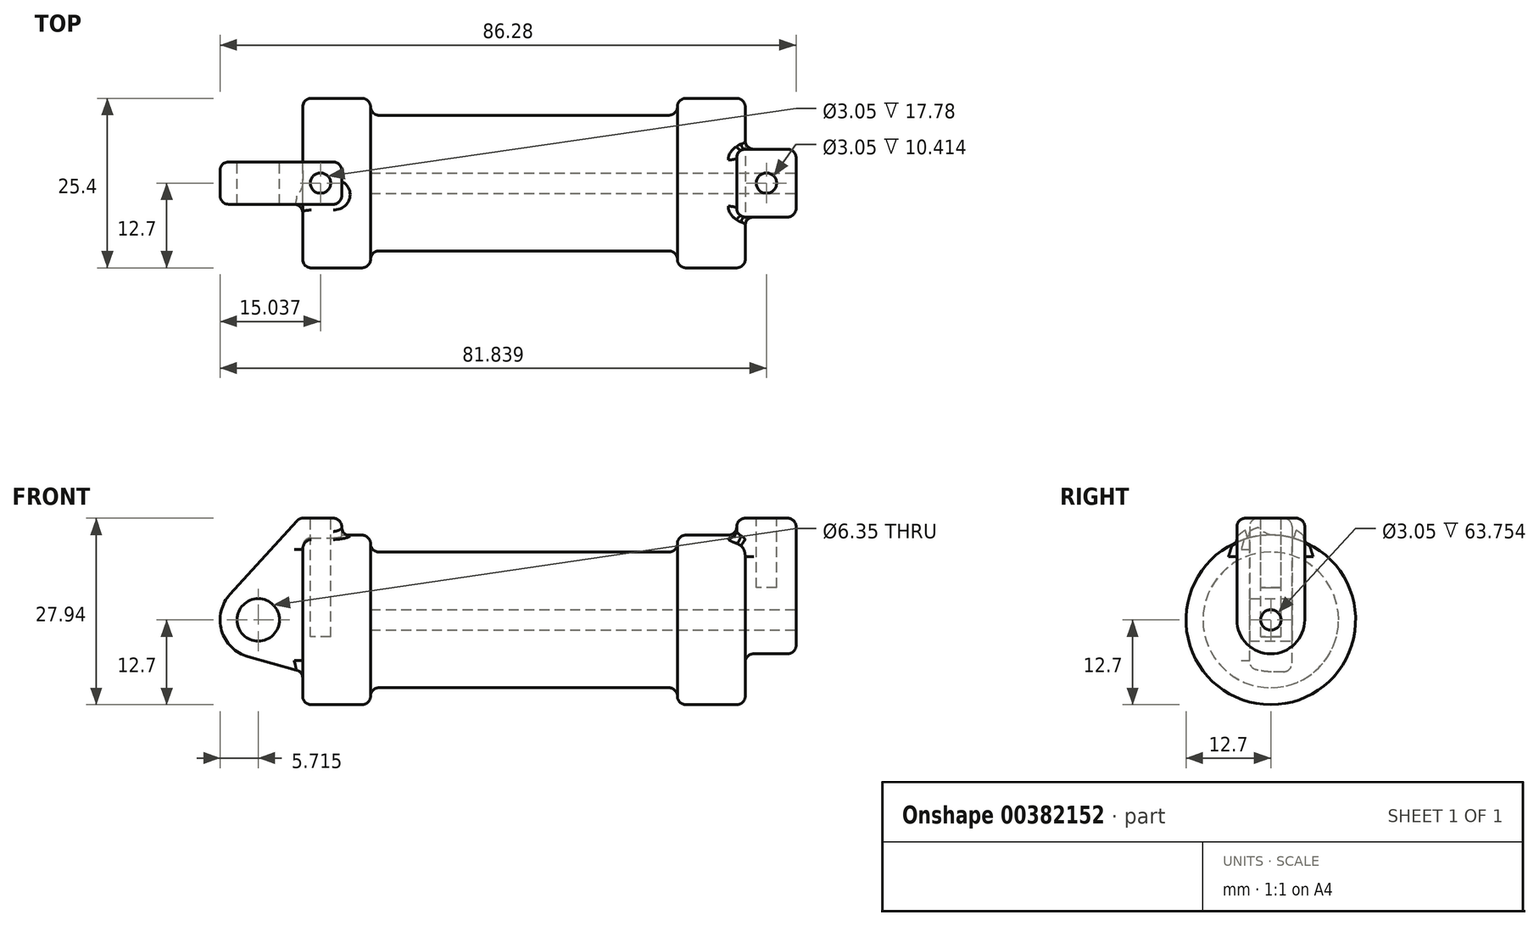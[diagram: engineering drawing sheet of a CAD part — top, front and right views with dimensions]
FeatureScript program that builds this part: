
annotation { "Feature Type Name" : "Feature", "Feature Type Description" : "" }
export const myFeature = defineFeature(function(context is Context, id is Id, definition is map)
    precondition{}
    {
        {
            var Q0;
            Q0=qCreatedBy(makeId("Front.planeOp"),FACE);
            var sketch = newSketch(context, id + "F0", { "sketchPlane" : qUnion([Q0])});
            skLineSegment(sketch, "E0", {"start": v(0, 0) * mm, "end": v(0, 12.7) * mm});
            skLineSegment(sketch, "E1", {"start": v(0, 12.7) * mm, "end": v(10.16, 12.7) * mm});
            skLineSegment(sketch, "E2", {"start": v(10.16, 12.7) * mm, "end": v(10.16, 10.16) * mm});
            skLineSegment(sketch, "E3", {"start": v(10.16, 10.16) * mm, "end": v(56.13, 10.16) * mm});
            skLineSegment(sketch, "E4", {"start": v(56.13, 10.16) * mm, "end": v(56.13, 12.7) * mm});
            skLineSegment(sketch, "E5", {"start": v(56.13, 12.7) * mm, "end": v(66.3, 12.7) * mm});
            skLineSegment(sketch, "E6", {"start": v(66.3, 12.7) * mm, "end": v(66.3, 0) * mm});
            skLineSegment(sketch, "E7", {"start": v(66.3, 0) * mm, "end": v(0, 0) * mm});
            skLineSegment(sketch, "E8", {"start": v(5.84, 15.24) * mm, "end": v(-0.5, 15.24) * mm});
            skLineSegment(sketch, "E9", {"start": v(-0.5, 15.24) * mm, "end": v(-10.88, 3.85) * mm});
            skLineSegment(sketch, "E10", {"start": v(0, 0) * mm, "end": v(-6.65, 0) * mm});
            skCircle(sketch, "E11", {"center": v(-6.65, 0) * mm, "radius": 5.72 * mm});
            skCircle(sketch, "E12", {"center": v(-6.65, 0) * mm, "radius": 3.18 * mm});
            skLineSegment(sketch, "E13", {"start": v(5.84, 15.24) * mm, "end": v(5.84, -9.4) * mm});
            skLineSegment(sketch, "E14", {"start": v(5.84, -9.4) * mm, "end": v(-8.18, -5.5) * mm});
            skSolve(sketch);
        }
        {
            var Q0;
            {var subQ1=sQuery(id+"F0.wireOp",EDGE,"E0");Q0=makeQuery(id+"F0.imprint","IMPRINT",FACE,{"disambiguationData":[TD([[makeQuery(id+"F0.imprint","IMPRINT",EDGE,{"derivedFrom":subQ1}),1.0]])]});}
            var Q1;
            {var subQ0=sQuery(id+"F0.wireOp",EDGE,"E14");Q1=makeQuery(id+"F0.imprint","IMPRINT",FACE,{"disambiguationData":[TD([[makeQuery(id+"F0.imprint","IMPRINT",EDGE,{"derivedFrom":subQ0}),-1.0]])]});}
            var Q2;
            {var subQ5=sQuery(id+"F0.wireOp",EDGE,"E12");Q2=makeQuery(id+"F0.imprint","IMPRINT",FACE,{"disambiguationData":[TD([[makeQuery(id+"F0.imprint","IMPRINT",EDGE,{"derivedFrom":subQ5}),-1.0]])]});}
            var Q3;
            {var subQ0=sQuery(id+"F0.wireOp",EDGE,"E0");Q3=makeQuery(id+"F0.imprint","IMPRINT",FACE,{"disambiguationData":[TD([[makeQuery(id+"F0.imprint","IMPRINT",EDGE,{"derivedFrom":subQ0}),-1.0]])]});}
            extrude(context, id + "F1", {"entities" : qUnion([Q0, Q1, Q2, Q3]), "endBound" : BoundingType.SYMMETRIC, "depth" : 6.35 * mm});
        }
        {
            var Q0;
            {var subQ0=sQuery(id+"F0.wireOp",EDGE,"E0");Q0=makeQuery(id+"F0.imprint","IMPRINT",FACE,{"disambiguationData":[TD([[makeQuery(id+"F0.imprint","IMPRINT",EDGE,{"derivedFrom":subQ0}),-1.0]])]});}
            var Q1;
            {var subQ0=sQuery(id+"F0.wireOp",EDGE,"E2");Q1=makeQuery(id+"F0.imprint","IMPRINT",FACE,{"disambiguationData":[TD([[makeQuery(id+"F0.imprint","IMPRINT",EDGE,{"derivedFrom":subQ0}),-1.0]])]});}
            var Q2;
            Q2=sQuery(id+"F0.wireOp",EDGE,"E7");
            revolve(context, id + "F2", {"operationType" : NewBodyOperationType.ADD, "entities" : qUnion([Q0, Q1]), "axis" : qUnion([Q2]), "revolveType" : RevolveType.FULL});
        }
        {
            var Q0;
            Q0=makeQuery(id+"F2.opRevolve","SWEPT_FACE",FACE,{"disambiguationData":[OSD([sQuery(id+"F0.wireOp",EDGE,"E6")])]});
            var sketch = newSketch(context, id + "F3", { "sketchPlane" : qUnion([Q0])});
            skCircle(sketch, "E15", {"center": v(0, 0) * mm, "radius": 1.52 * mm});
            skCircle(sketch, "E16", {"center": v(0, 0) * mm, "radius": 5.08 * mm});
            skLineSegment(sketch, "E17", {"start": v(-5.08, 0) * mm, "end": v(-5.08, 15.24) * mm});
            skLineSegment(sketch, "E18", {"start": v(5.08, 0) * mm, "end": v(5.08, 15.24) * mm});
            skLineSegment(sketch, "E19", {"start": v(5.08, 15.24) * mm, "end": v(-5.08, 15.24) * mm});
            skSolve(sketch);
        }
        {
            var Q0;
            Q0=makeQuery(id+"F3.imprint","IMPRINT",FACE,{"disambiguationData":[TD([[makeQuery(id+"F3.imprint","IMPRINT",EDGE,{"derivedFrom":sQuery(id+"F3.wireOp",EDGE,"E15")}),1.0]])]});
            var Q1;
            Q1=sQuery(id+"F3.wireOp",EDGE,"E15");
            var Q2;
            Q2=makeQuery(id+"F2.opRevolve","SWEPT_FACE",FACE,{"disambiguationData":[OSD([sQuery(id+"F0.wireOp",EDGE,"E2")])]});
            extrude(context, id + "F4", {"entities" : qUnion([Q0]), "operationType" : NewBodyOperationType.REMOVE, "surfaceEntities" : qUnion([Q1]), "endBound" : BoundingType.UP_TO_SURFACE, "oppositeDirection" : true, "endBoundEntityFace" : qUnion([Q2]), "depth" : 25.4 * mm});
        }
        {
            var Q0;
            Q0 = qSketchRegion(id + "F3", true);
            extrude(context, id + "F5", {"entities" : qUnion([Q0]), "operationType" : NewBodyOperationType.ADD, "depth" : 7.62 * mm, "hasSecondDirection" : true, "secondDirectionOppositeDirection" : true, "secondDirectionDepth" : 1.27 * mm});
        }
        {
            var Q0;
            Q0=makeQuery(id+"F1.opExtrude","SWEPT_FACE",FACE,{"disambiguationData":[OSD([sQuery(id+"F0.wireOp",EDGE,"E8")])]});
            var sketch = newSketch(context, id + "F6", { "sketchPlane" : qUnion([Q0])});
            skCircle(sketch, "E20", {"center": v(2.67, 0) * mm, "radius": 1.52 * mm});
            skPoint(sketch, "E20.centerSnap0", {"position": v(-0.5, 0) * mm});
            skPoint(sketch, "E20.centerSnap1", {"position": v(2.67, 3.18) * mm});
            skSolve(sketch);
        }
        {
            var Q0;
            Q0=makeQuery(id+"F6.imprint","IMPRINT",FACE,{"disambiguationData":[TD([[makeQuery(id+"F6.imprint","IMPRINT",EDGE,{"derivedFrom":sQuery(id+"F6.wireOp",EDGE,"E20")}),1.0]])]});
            extrude(context, id + "F7", {"entities" : qUnion([Q0]), "operationType" : NewBodyOperationType.REMOVE, "oppositeDirection" : true, "depth" : 17.78 * mm});
        }
        {
            var Q0;
            Q0=makeQuery(id+"F5.opExtrude","SWEPT_FACE",FACE,{"disambiguationData":[OSD([sQuery(id+"F3.wireOp",EDGE,"E19")])]});
            var sketch = newSketch(context, id + "F8", { "sketchPlane" : qUnion([Q0])});
            skCircle(sketch, "E21", {"center": v(69.47, 0) * mm, "radius": 1.52 * mm});
            skPoint(sketch, "E21.centerSnap0", {"position": v(69.47, 5.08) * mm});
            skPoint(sketch, "E21.centerSnap1", {"position": v(65.02, 0) * mm});
            skSolve(sketch);
        }
        {
            var Q0;
            Q0=makeQuery(id+"F8.imprint","IMPRINT",FACE,{"disambiguationData":[TD([[makeQuery(id+"F8.imprint","IMPRINT",EDGE,{"derivedFrom":sQuery(id+"F8.wireOp",EDGE,"E21")}),1.0]])]});
            extrude(context, id + "F9", {"entities" : qUnion([Q0]), "operationType" : NewBodyOperationType.REMOVE, "oppositeDirection" : true, "depth" : 10.4 * mm});
        }
        {
            var Q0;
            Q0=makeQuery(id+"F2.opRevolve","SWEPT_EDGE",EDGE,{"disambiguationData":[OSD([sQuery(id+"F0.wireOp",EDGE,"E2"),sQuery(id+"F0.wireOp",EDGE,"E3")])]});
            var Q1;
            Q1=makeQuery(id+"F2.opRevolve","SWEPT_FACE",FACE,{"disambiguationData":[OSD([sQuery(id+"F0.wireOp",EDGE,"E4")])]});
            var Q2;
            Q2=makeQuery(id+"F2.opRevolve","SWEPT_EDGE",EDGE,{"disambiguationData":[OSD([sQuery(id+"F0.wireOp",EDGE,"E5"),sQuery(id+"F0.wireOp",EDGE,"E6")])]});
            var Q3;
            Q3=makeQuery(id+"F2.opRevolve","SWEPT_EDGE",EDGE,{"disambiguationData":[OSD([sQuery(id+"F0.wireOp",EDGE,"E0"),sQuery(id+"F0.wireOp",EDGE,"E1")])]});
            var Q4;
            Q4=makeQuery(id+"F2.opRevolve","SWEPT_EDGE",EDGE,{"disambiguationData":[OSD([sQuery(id+"F0.wireOp",EDGE,"E1"),sQuery(id+"F0.wireOp",EDGE,"E2")])]});
            fillet(context, id + "F10", {"entities" : qUnion([Q0, Q1, Q2, Q3, Q4]), "radius" : 1.27 * mm, "tangentPropagation" : true, "allowEdgeOverflow" : false});
        }
        {
            var Q0;
            Q0=makeQuery(id+"F1.opExtrude","CAP_EDGE",EDGE,{"disambiguationData":[OSD([sQuery(id+"F0.wireOp",EDGE,"E8")])],"isStart":false});
            var Q1;
            Q1=makeQuery(id+"F1.opExtrude","CAP_EDGE",EDGE,{"disambiguationData":[OSD([sQuery(id+"F0.wireOp",EDGE,"E8")])],"isStart":true});
            var Q2;
            Q2=makeQuery(id+"F1.opExtrude","SWEPT_EDGE",EDGE,{"disambiguationData":[OSD([sQuery(id+"F0.wireOp",EDGE,"E8"),sQuery(id+"F0.wireOp",EDGE,"E13")])]});
            var Q3;
            Q3=makeQuery(id+"F1.opExtrude","SWEPT_EDGE",EDGE,{"disambiguationData":[OSD([sQuery(id+"F0.wireOp",EDGE,"E8"),sQuery(id+"F0.wireOp",EDGE,"E9")])]});
            var Q4;
            Q4=makeQuery(id+"F1.opExtrude","CAP_EDGE",EDGE,{"disambiguationData":[OSD([sQuery(id+"F0.wireOp",EDGE,"E9")])],"isStart":false});
            var Q5;
            Q5=makeQuery(id+"F1.opExtrude","CAP_EDGE",EDGE,{"disambiguationData":[OSD([sQuery(id+"F0.wireOp",EDGE,"E9")])],"isStart":true});
            var Q6;
            Q6=makeQuery(id+"F1.opExtrude","SWEPT_EDGE",EDGE,{"disambiguationData":[OSD([sQuery(id+"F0.wireOp",EDGE,"E9"),sQuery(id+"F0.wireOp",EDGE,"E11")])]});
            var Q7;
            Q7=makeQuery(id+"F1.opExtrude","CAP_EDGE",EDGE,{"disambiguationData":[OSD([sQuery(id+"F0.wireOp",EDGE,"E13")])],"isStart":false});
            var Q8;
            Q8=makeQuery(id+"F1.opExtrude","CAP_EDGE",EDGE,{"disambiguationData":[OSD([sQuery(id+"F0.wireOp",EDGE,"E13")])],"isStart":true});
            var Q9;
            Q9=makeQuery(id+"F2.boolean.opBoolean","INTERSECT",EDGE,{"derivedFrom":[makeQuery(id+"F1.opExtrude","CAP_FACE",FACE,{"disambiguationData":[OSD([sQuery(id+"F0.wireOp",EDGE,"E8"),sQuery(id+"F0.wireOp",EDGE,"E9"),sQuery(id+"F0.wireOp",EDGE,"E11"),sQuery(id+"F0.wireOp",EDGE,"E12"),sQuery(id+"F0.wireOp",EDGE,"E13"),sQuery(id+"F0.wireOp",EDGE,"E14")])],"isStart":false}),makeQuery(id+"F2.opRevolve","SWEPT_FACE",FACE,{"disambiguationData":[OSD([sQuery(id+"F0.wireOp",EDGE,"E1")])]})]});
            fillet(context, id + "F11", {"entities" : qUnion([Q0, Q1, Q2, Q3, Q4, Q5, Q6, Q7, Q8, Q9]), "radius" : 1.27 * mm, "tangentPropagation" : true, "allowEdgeOverflow" : false});
        }
        {
            var Q0;
            Q0=makeQuery(id+"F5.opExtrude","SWEPT_FACE",FACE,{"disambiguationData":[OSD([sQuery(id+"F3.wireOp",EDGE,"E16")])]});
            var Q1;
            Q1=makeQuery(id+"F5.opExtrude","CAP_FACE",FACE,{"disambiguationData":[OSD([sQuery(id+"F3.wireOp",EDGE,"E15"),sQuery(id+"F3.wireOp",EDGE,"E16"),sQuery(id+"F3.wireOp",EDGE,"E17"),sQuery(id+"F3.wireOp",EDGE,"E18"),sQuery(id+"F3.wireOp",EDGE,"E19")])],"isStart":true});
            var Q2;
            Q2=makeQuery(id+"F5.opExtrude","CAP_EDGE",EDGE,{"disambiguationData":[OSD([sQuery(id+"F3.wireOp",EDGE,"E19")])],"isStart":false});
            var Q3;
            Q3=makeQuery(id+"F5.opExtrude","SWEPT_EDGE",EDGE,{"disambiguationData":[OSD([sQuery(id+"F3.wireOp",EDGE,"E17"),sQuery(id+"F3.wireOp",EDGE,"E19")])]});
            var Q4;
            Q4=makeQuery(id+"F5.opExtrude","SWEPT_EDGE",EDGE,{"disambiguationData":[OSD([sQuery(id+"F3.wireOp",EDGE,"E18"),sQuery(id+"F3.wireOp",EDGE,"E19")])]});
            fillet(context, id + "F12", {"entities" : qUnion([Q0, Q1, Q2, Q3, Q4]), "radius" : 1.27 * mm, "tangentPropagation" : true, "allowEdgeOverflow" : false});
        }
    });
